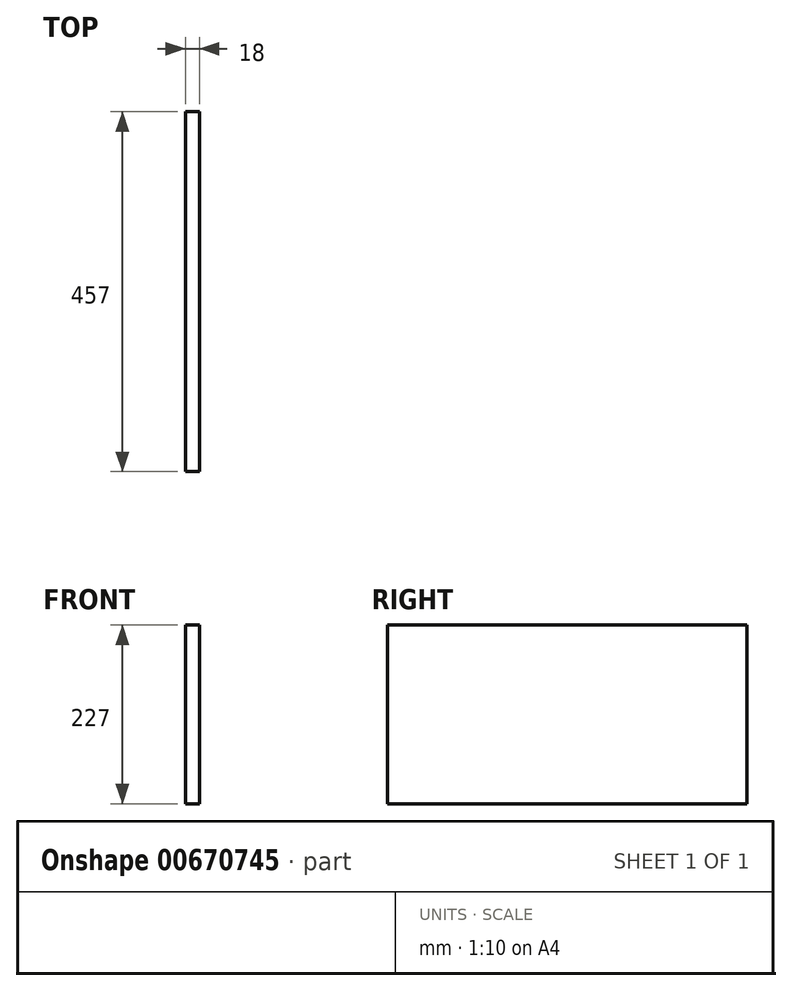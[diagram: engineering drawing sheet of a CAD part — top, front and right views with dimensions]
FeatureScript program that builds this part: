
annotation { "Feature Type Name" : "Feature", "Feature Type Description" : "" }
export const myFeature = defineFeature(function(context is Context, id is Id, definition is map)
    precondition{}
    {
        {
            var Q0;
            Q0=qCreatedBy(makeId("Right.planeOp"),FACE);
            var sketch = newSketch(context, id + "F0", { "sketchPlane" : qUnion([Q0])});
            skLineSegment(sketch, "E0.bottom", {"start": v(228.5, 113.5) * mm, "end": v(-228.5, 113.5) * mm});
            skLineSegment(sketch, "E0.top", {"start": v(228.5, -113.5) * mm, "end": v(-228.5, -113.5) * mm});
            skLineSegment(sketch, "E0.left", {"start": v(228.5, 113.5) * mm, "end": v(228.5, -113.5) * mm});
            skLineSegment(sketch, "E0.right", {"start": v(-228.5, 113.5) * mm, "end": v(-228.5, -113.5) * mm});
            skPoint(sketch, "E0.middle", {"position": v(0, 0) * mm});
            skSolve(sketch);
        }
        {
            var Q0;
            Q0 = qSketchRegion(id + "F0", true);
            extrude(context, id + "F1", {"entities" : qUnion([Q0]), "endBound" : BoundingType.SYMMETRIC, "depth" : 18 * mm, "offsetDistance" : 25 * mm});
        }
    });
